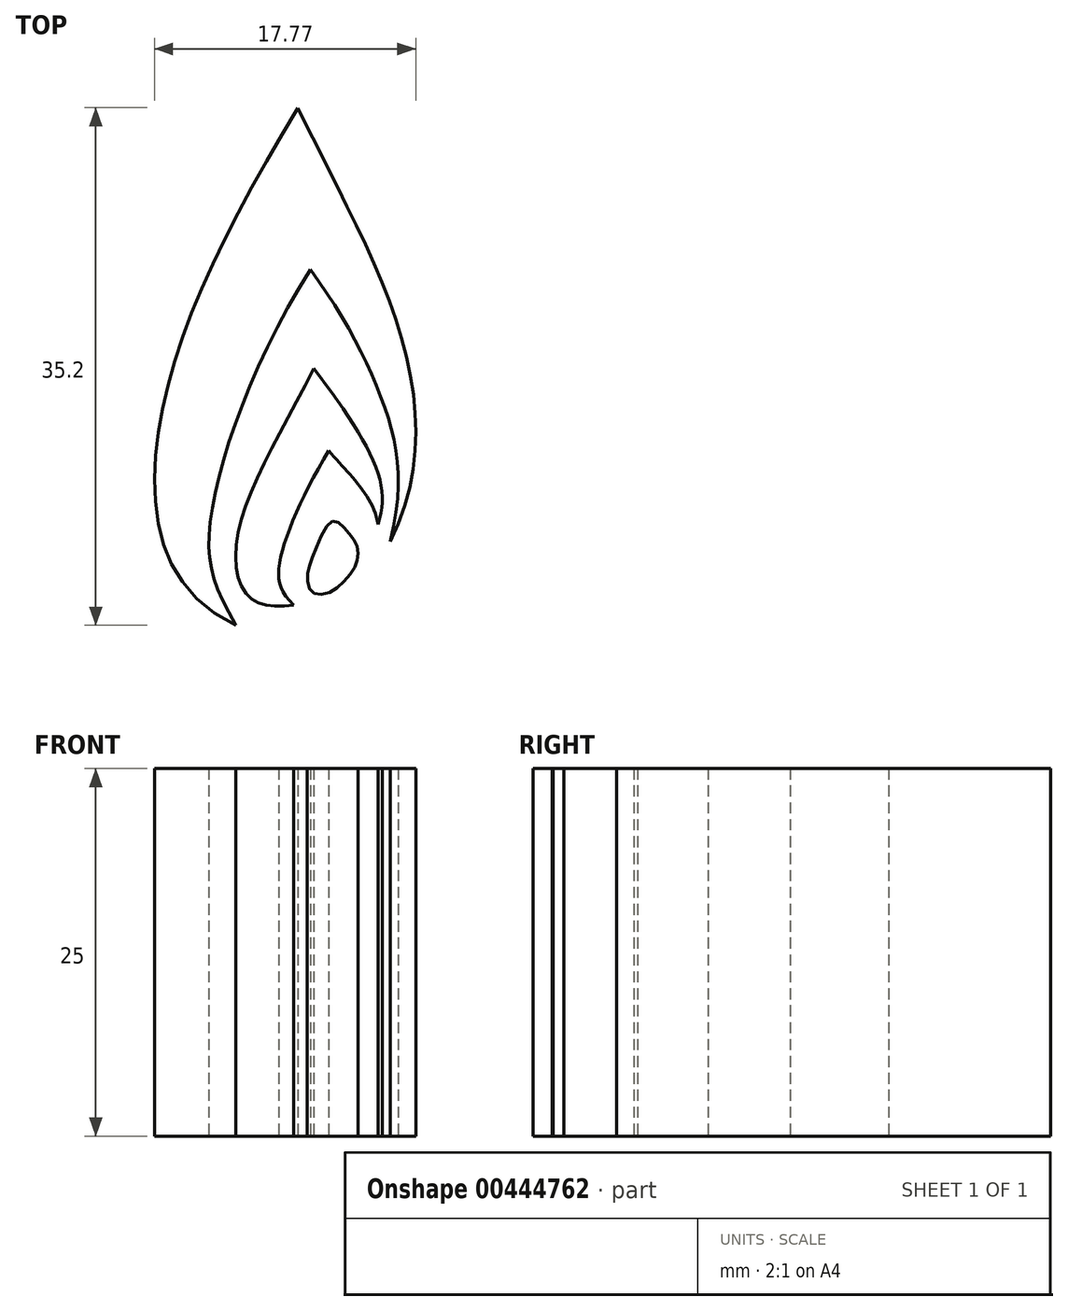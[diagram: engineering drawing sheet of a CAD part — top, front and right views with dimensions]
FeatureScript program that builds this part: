
annotation { "Feature Type Name" : "Feature", "Feature Type Description" : "" }
export const myFeature = defineFeature(function(context is Context, id is Id, definition is map)
    precondition{}
    {
        {
            var Q0;
            Q0=qCreatedBy(makeId("Top.planeOp"),FACE);
            var sketch = newSketch(context, id + "F0", { "sketchPlane" : qUnion([Q0])});
            skFitSpline(sketch, "E0", {"points": [v(-53, 20.79) * mm, v(-62.5, -1.35) * mm, v(-57.23, -14.41) * mm], "startDerivative": vector(-25.61, -42.58) * mm, "endDerivative": vector(36.43, -17.59) * mm});
            skFitSpline(sketch, "E1", {"points": [v(-53, 20.79) * mm, v(-45.86, 4.82) * mm, v(-46.7, -8.73) * mm], "startDerivative": vector(15.36, -31.74) * mm, "endDerivative": vector(-13.95, -27.9) * mm});
            skFitSpline(sketch, "E2", {"points": [v(-57.23, -14.41) * mm, v(-58.99, -7.64) * mm, v(-52.15, 9.78) * mm], "startDerivative": vector(-11.95, 21.52) * mm, "endDerivative": vector(18.71, 29.24) * mm});
            skFitSpline(sketch, "E3", {"points": [v(-52.15, 9.78) * mm, v(-47.13, 0.52) * mm, v(-46.7, -8.73) * mm], "startDerivative": vector(13.71, -18.64) * mm, "endDerivative": vector(-6, -24.74) * mm});
            skFitSpline(sketch, "E4", {"points": [v(-53.27, -13.05) * mm, v(-54.28, -10.41) * mm, v(-50.9, -2.54) * mm], "startDerivative": vector(-7.64, 7.64) * mm, "endDerivative": vector(8.6, 14.1) * mm});
            skFitSpline(sketch, "E5", {"points": [v(-50.9, -2.54) * mm, v(-47.55, -7.56) * mm], "startDerivative": vector(3.9, -4.7) * mm, "endDerivative": vector(0.9, -6.06) * mm});
            skFitSpline(sketch, "E6", {"points": [v(-47.55, -7.56) * mm, v(-47.55, -4.06) * mm, v(-51.91, 3.06) * mm], "startDerivative": vector(2.74, 8.93) * mm, "endDerivative": vector(-9.76, 12.82) * mm});
            skFitSpline(sketch, "E7", {"points": [v(-51.91, 3.06) * mm, v(-57.03, -7.97) * mm, v(-56.37, -12.43) * mm, v(-53.27, -13.05) * mm], "startDerivative": vector(-13.29, -26.33) * mm, "endDerivative": vector(15.45, 1.93) * mm});
            skFitSpline(sketch, "E8", {"points": [v(-50.64, -7.32) * mm, v(-51.84, -9.37) * mm, v(-52.34, -10.96) * mm, v(-52.07, -12.12) * mm, v(-50.98, -12.23) * mm, v(-49.55, -11.07) * mm, v(-48.93, -9.91) * mm, v(-49.05, -8.87) * mm, v(-49.82, -7.82) * mm, v(-50.64, -7.32) * mm]});
            skSolve(sketch);
        }
        {
            var Q0;
            Q0 = qSketchRegion(id + "F0", true);
            extrude(context, id + "F1", {"entities" : qUnion([Q0]), "depth" : 25 * mm});
        }
    });
